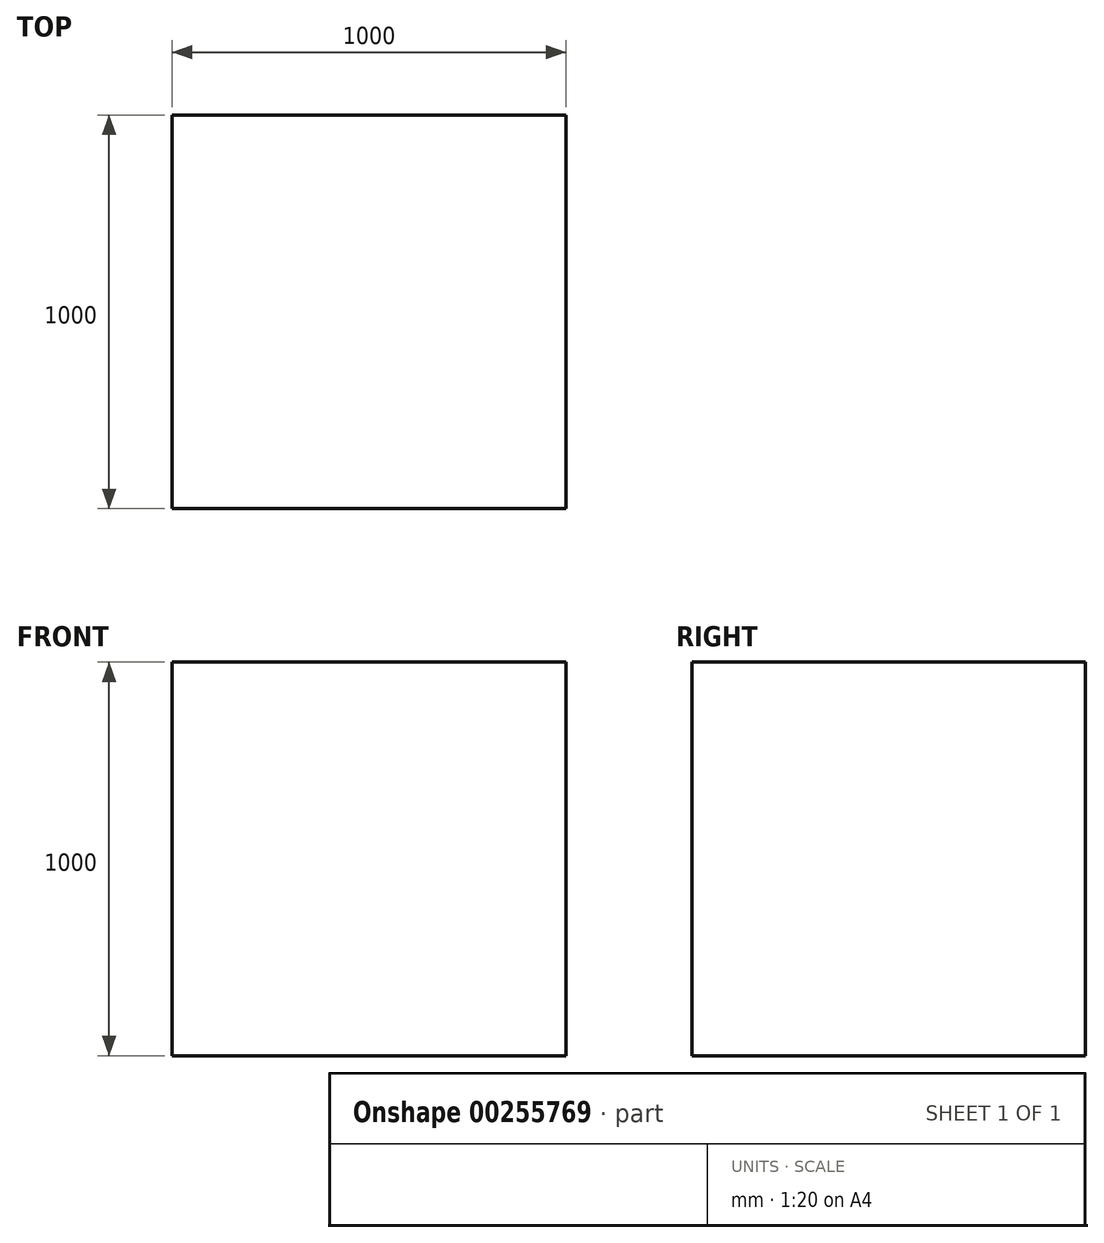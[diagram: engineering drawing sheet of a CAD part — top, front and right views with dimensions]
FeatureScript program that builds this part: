
annotation { "Feature Type Name" : "Feature", "Feature Type Description" : "" }
export const myFeature = defineFeature(function(context is Context, id is Id, definition is map)
    precondition{}
    {
        {
            var Q0;
            Q0=qCreatedBy(makeId("Front.planeOp"),FACE);
            var sketch = newSketch(context, id + "F0", { "sketchPlane" : qUnion([Q0])});
            skLineSegment(sketch, "E0.bottom", {"start": v(0, 0) * mm, "end": v(1000, 0) * mm});
            skLineSegment(sketch, "E0.top", {"start": v(0, 1000) * mm, "end": v(1000, 1000) * mm});
            skLineSegment(sketch, "E0.left", {"start": v(0, 0) * mm, "end": v(0, 1000) * mm});
            skLineSegment(sketch, "E0.right", {"start": v(1000, 0) * mm, "end": v(1000, 1000) * mm});
            skSolve(sketch);
        }
        {
            var Q0;
            Q0=makeQuery(id+"F0.imprint","IMPRINT",FACE,{"disambiguationData":[TD([[makeQuery(id+"F0.imprint","IMPRINT",EDGE,{"derivedFrom":sQuery(id+"F0.wireOp",EDGE,"E0.bottom")}),1.0]])]});
            extrude(context, id + "F1", {"entities" : qUnion([Q0]), "oppositeDirection" : true, "depth" : 1000 * mm, "offsetDistance" : 25 * mm});
        }
    });
